# Revit family: Electronics_Amplifier_Biamp_Tesira_4-Channel-300W_AMP-4300R-CV__
name_source: partatom
category: Communication Devices
units: mm (PartAtom-declared; Revit-internal decimal feet)

## family parameters
Cut with Voids When Loaded = Yes
Host = Face
Maintain Annotation Orientation = No
OmniClass Number = 23.85.10.11.14.14.17
OmniClass Title = Sound Amplifiers
Part Type = Normal
Room Calculation Point = No
Round Connector Dimension = Use Diameter
Shared = No

## types (1)
- AMP-4350R
    Altitude = 0-10,000 ft (0-3000m) MSL
    Apparent Load = 660 VA
    Balanced Input Impedance = 8 kohm
    Case = Yes
    Compliance = FCC Part 15B (USA) CE Marked (Europe) UL and C-UL listed (USA and Canada) RCM (Australia) EAC (Eurasian Customs Union) CCC (China) KCC (Korea) RoHS Directive (Europe)
    Connector Description = 100-240VAC 50/60Hz
    Cooling = Variable speed fan
    Current = 6 A
    Current Draw = 5.5–2.3A
    Default Elevation = 48 "
    Depth = 17.4 "
    Description = Tesira® AMP-4350R 4-Channel, 350W Amplifier
    Dual AVB/TSN Input = RJ-45 (CAT-5 or higher) inputs; primary and secondary
    Dynamic Range = > 100dB
    Frequency Response = ± 1dB
    Height = 3.5 "
    Housing Material = Biamp - Metal - Silver
    Humidity = 0-95% relative humidity (non-condensing)
    Manufacturer = Biamp
    Minimum Operational Load = 2 ohm
    Model = Tesira AMP-4350R
    Number of Channels = 4
    Number of Poles = 1
    Optional Analog Cards = Tesira EX-MOD cards: EIC-4, EIOC-4, EOC-4
    Power Factor = 1
    Product Documentation Link = https://downloads.biamp.com
    Product Page URL = https://www.biamp.com
    Product data url = https://www.bimobject.com
    Single Channel = 70V/100V: 300W
    THD+N = 20Hz-20kHz, at rated power: < 0.3%
    Temperature Range = 32 - 104° F (0 - 40° C)
    URL = https://www.biamp.com
    Voltage = 120 V
    Weight = 20.60 lbf
    Width = 19 "

## geometry (parser evidence)
native form markers: Sweep x2
no freeform markers — native parametric forms only
